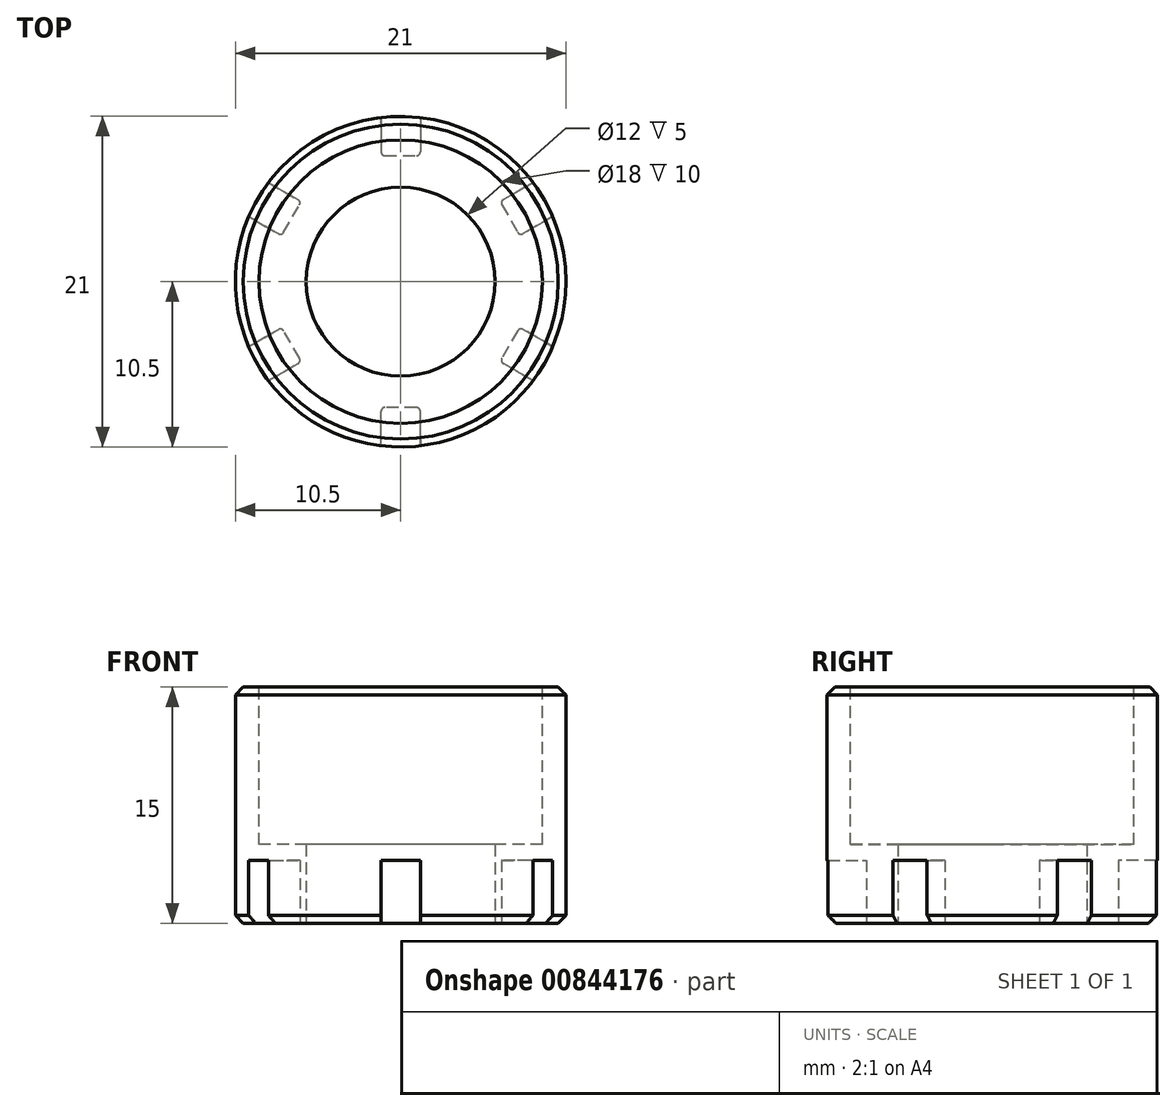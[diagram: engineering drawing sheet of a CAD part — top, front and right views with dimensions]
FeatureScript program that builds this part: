
annotation { "Feature Type Name" : "Feature", "Feature Type Description" : "" }
export const myFeature = defineFeature(function(context is Context, id is Id, definition is map)
    precondition{}
    {
        {
            var Q0;
            Q0=qCreatedBy(makeId("Top.planeOp"),FACE);
            var sketch = newSketch(context, id + "F0", { "sketchPlane" : qUnion([Q0])});
            skCircle(sketch, "E0", {"center": v(0, 0) * mm, "radius": 10.5 * mm});
            skCircle(sketch, "E1", {"center": v(0, 0) * mm, "radius": 6 * mm});
            skSolve(sketch);
        }
        {
            var Q0;
            Q0=makeQuery(id+"F0.imprint","IMPRINT",FACE,{"disambiguationData":[TD([[makeQuery(id+"F0.imprint","IMPRINT",EDGE,{"derivedFrom":sQuery(id+"F0.wireOp",EDGE,"E0")}),1.0]])]});
            extrude(context, id + "F1", {"entities" : qUnion([Q0]), "depth" : 15 * mm, "offsetDistance" : 25 * mm});
        }
        {
            var Q0;
            Q0=makeQuery(id+"F1.opExtrude","CAP_FACE",FACE,{"disambiguationData":[OSD([sQuery(id+"F0.wireOp",EDGE,"E0"),sQuery(id+"F0.wireOp",EDGE,"E1")])],"isStart":false});
            var sketch = newSketch(context, id + "F2", { "sketchPlane" : qUnion([Q0])});
            skCircle(sketch, "E2", {"center": v(0, 0) * mm, "radius": 9 * mm});
            skSolve(sketch);
        }
        {
            var Q0;
            Q0=makeQuery(id+"F2.imprint","IMPRINT",FACE,{"disambiguationData":[TD([[makeQuery(id+"F2.imprint","IMPRINT",EDGE,{"derivedFrom":sQuery(id+"F2.wireOp",EDGE,"E2")}),1.0]])]});
            extrude(context, id + "F3", {"entities" : qUnion([Q0]), "operationType" : NewBodyOperationType.REMOVE, "oppositeDirection" : true, "depth" : 10 * mm, "offsetDistance" : 25 * mm});
        }
        {
            var Q0;
            Q0=makeQuery(id+"F1.opExtrude","CAP_FACE",FACE,{"disambiguationData":[OSD([sQuery(id+"F0.wireOp",EDGE,"E0"),sQuery(id+"F0.wireOp",EDGE,"E1")])],"isStart":true});
            var sketch = newSketch(context, id + "F4", { "sketchPlane" : qUnion([Q0])});
            skLineSegment(sketch, "E3", {"start": v(0, 14.48) * mm, "end": v(0, 7.94) * mm, "construction": true});
            skLineSegment(sketch, "E4.bottom", {"start": v(1.25, 13) * mm, "end": v(-1.25, 13) * mm});
            skLineSegment(sketch, "E4.top", {"start": v(1, 8) * mm, "end": v(-1, 8) * mm});
            skLineSegment(sketch, "E4.left", {"start": v(1.25, 13) * mm, "end": v(1.25, 8.25) * mm});
            skLineSegment(sketch, "E4.right", {"start": v(-1.25, 13) * mm, "end": v(-1.25, 8.25) * mm});
            skPoint(sketch, "E4.middle", {"position": v(0, 10.5) * mm});
            skPoint(sketch, "E5.visualSharp", {"position": v(-1.25, 8) * mm});
            skArc(sketch, "E5.filletArc", {"start": v(-1.25, 8.25) * mm, "mid": v(-1.18, 8.07) * mm, "end": v(-1, 8) * mm});
            skPoint(sketch, "E6.visualSharp", {"position": v(1.25, 8) * mm});
            skArc(sketch, "E6.filletArc", {"start": v(1, 8) * mm, "mid": v(1.18, 8.07) * mm, "end": v(1.25, 8.25) * mm});
            skLineSegment(sketch, "E7.1.0", {"start": v(-10.63, 7.58) * mm, "end": v(-6.52, 5.2) * mm});
            skPoint(sketch, "E7.1.1", {"position": v(-9.1, 5.25) * mm});
            skPoint(sketch, "E7.1.2", {"position": v(-7.55, 2.92) * mm});
            skPoint(sketch, "E7.1.3", {"position": v(-6.3, 5.08) * mm});
            skLineSegment(sketch, "E7.1.4", {"start": v(-12.54, 7.24) * mm, "end": v(-6.88, 3.97) * mm, "construction": true});
            skLineSegment(sketch, "E7.1.5", {"start": v(-10.63, 7.58) * mm, "end": v(-11.88, 5.42) * mm});
            skLineSegment(sketch, "E7.1.6", {"start": v(-11.88, 5.42) * mm, "end": v(-7.77, 3.04) * mm});
            skLineSegment(sketch, "E7.1.7", {"start": v(-6.43, 4.87) * mm, "end": v(-7.43, 3.13) * mm});
            skArc(sketch, "E7.1.8", {"start": v(-7.77, 3.04) * mm, "mid": v(-7.58, 3.02) * mm, "end": v(-7.43, 3.13) * mm});
            skArc(sketch, "E7.1.9", {"start": v(-6.43, 4.87) * mm, "mid": v(-6.4, 5.06) * mm, "end": v(-6.52, 5.2) * mm});
            skLineSegment(sketch, "E7.2.0", {"start": v(-11.88, -5.42) * mm, "end": v(-7.77, -3.04) * mm});
            skPoint(sketch, "E7.2.1", {"position": v(-9.1, -5.25) * mm});
            skPoint(sketch, "E7.2.2", {"position": v(-6.3, -5.08) * mm});
            skPoint(sketch, "E7.2.3", {"position": v(-7.55, -2.92) * mm});
            skLineSegment(sketch, "E7.2.4", {"start": v(-12.54, -7.24) * mm, "end": v(-6.88, -3.97) * mm, "construction": true});
            skLineSegment(sketch, "E7.2.5", {"start": v(-11.88, -5.42) * mm, "end": v(-10.63, -7.58) * mm});
            skLineSegment(sketch, "E7.2.6", {"start": v(-10.63, -7.58) * mm, "end": v(-6.52, -5.2) * mm});
            skLineSegment(sketch, "E7.2.7", {"start": v(-7.43, -3.13) * mm, "end": v(-6.43, -4.87) * mm});
            skArc(sketch, "E7.2.8", {"start": v(-6.52, -5.2) * mm, "mid": v(-6.4, -5.06) * mm, "end": v(-6.43, -4.87) * mm});
            skArc(sketch, "E7.2.9", {"start": v(-7.43, -3.13) * mm, "mid": v(-7.58, -3.02) * mm, "end": v(-7.77, -3.04) * mm});
            skLineSegment(sketch, "E7.3.0", {"start": v(-1.25, -13) * mm, "end": v(-1.25, -8.25) * mm});
            skPoint(sketch, "E7.3.1", {"position": v(0, -10.5) * mm});
            skPoint(sketch, "E7.3.2", {"position": v(1.25, -8) * mm});
            skPoint(sketch, "E7.3.3", {"position": v(-1.25, -8) * mm});
            skLineSegment(sketch, "E7.3.4", {"start": v(0, -14.48) * mm, "end": v(0, -7.94) * mm, "construction": true});
            skLineSegment(sketch, "E7.3.5", {"start": v(-1.25, -13) * mm, "end": v(1.25, -13) * mm});
            skLineSegment(sketch, "E7.3.6", {"start": v(1.25, -13) * mm, "end": v(1.25, -8.25) * mm});
            skLineSegment(sketch, "E7.3.7", {"start": v(-1, -8) * mm, "end": v(1, -8) * mm});
            skArc(sketch, "E7.3.8", {"start": v(1.25, -8.25) * mm, "mid": v(1.18, -8.07) * mm, "end": v(1, -8) * mm});
            skArc(sketch, "E7.3.9", {"start": v(-1, -8) * mm, "mid": v(-1.18, -8.07) * mm, "end": v(-1.25, -8.25) * mm});
            skLineSegment(sketch, "E7.4.0", {"start": v(10.63, -7.58) * mm, "end": v(6.52, -5.2) * mm});
            skPoint(sketch, "E7.4.1", {"position": v(9.1, -5.25) * mm});
            skPoint(sketch, "E7.4.2", {"position": v(7.55, -2.92) * mm});
            skPoint(sketch, "E7.4.3", {"position": v(6.3, -5.08) * mm});
            skLineSegment(sketch, "E7.4.4", {"start": v(12.54, -7.24) * mm, "end": v(6.88, -3.97) * mm, "construction": true});
            skLineSegment(sketch, "E7.4.5", {"start": v(10.63, -7.58) * mm, "end": v(11.88, -5.42) * mm});
            skLineSegment(sketch, "E7.4.6", {"start": v(11.88, -5.42) * mm, "end": v(7.77, -3.04) * mm});
            skLineSegment(sketch, "E7.4.7", {"start": v(6.43, -4.87) * mm, "end": v(7.43, -3.13) * mm});
            skArc(sketch, "E7.4.8", {"start": v(7.77, -3.04) * mm, "mid": v(7.58, -3.02) * mm, "end": v(7.43, -3.13) * mm});
            skArc(sketch, "E7.4.9", {"start": v(6.43, -4.87) * mm, "mid": v(6.4, -5.06) * mm, "end": v(6.52, -5.2) * mm});
            skLineSegment(sketch, "E7.5.0", {"start": v(11.88, 5.42) * mm, "end": v(7.77, 3.04) * mm});
            skPoint(sketch, "E7.5.1", {"position": v(9.1, 5.25) * mm});
            skPoint(sketch, "E7.5.2", {"position": v(6.3, 5.08) * mm});
            skPoint(sketch, "E7.5.3", {"position": v(7.55, 2.92) * mm});
            skLineSegment(sketch, "E7.5.4", {"start": v(12.54, 7.24) * mm, "end": v(6.88, 3.97) * mm, "construction": true});
            skLineSegment(sketch, "E7.5.5", {"start": v(11.88, 5.42) * mm, "end": v(10.63, 7.58) * mm});
            skLineSegment(sketch, "E7.5.6", {"start": v(10.63, 7.58) * mm, "end": v(6.52, 5.2) * mm});
            skLineSegment(sketch, "E7.5.7", {"start": v(7.43, 3.13) * mm, "end": v(6.43, 4.87) * mm});
            skArc(sketch, "E7.5.8", {"start": v(6.52, 5.2) * mm, "mid": v(6.4, 5.06) * mm, "end": v(6.43, 4.87) * mm});
            skArc(sketch, "E7.5.9", {"start": v(7.43, 3.13) * mm, "mid": v(7.58, 3.02) * mm, "end": v(7.77, 3.04) * mm});
            skPoint(sketch, "E7.center", {"position": v(0, 0) * mm});
            skSolve(sketch);
        }
        {
            var Q0;
            Q0=qSketchRegion(id+"F4",true);
            extrude(context, id + "F5", {"entities" : qUnion([Q0]), "operationType" : NewBodyOperationType.REMOVE, "oppositeDirection" : true, "depth" : 4 * mm, "offsetDistance" : 25 * mm});
        }
        {
            var Q0;
            {var subQ0=sQuery(id+"F0.wireOp",EDGE,"E0");Q0=makeQuery(id+"F5.boolean.opBoolean","SPLIT",EDGE,{"disambiguationData":[TD([makeQuery(id+"F5.opExtrude","SWEPT_FACE",FACE,{"disambiguationData":[OSD([sQuery(id+"F4.wireOp",EDGE,"E4.right")])]})])],"derivedFrom":makeQuery(id+"F1.opExtrude","CAP_EDGE",EDGE,{"disambiguationData":[OSD([subQ0])],"isStart":true})});}
            var Q1;
            {var subQ0=sQuery(id+"F0.wireOp",EDGE,"E0");Q1=makeQuery(id+"F5.boolean.opBoolean","SPLIT",EDGE,{"disambiguationData":[TD([makeQuery(id+"F5.opExtrude","SWEPT_FACE",FACE,{"disambiguationData":[OSD([sQuery(id+"F4.wireOp",EDGE,"E4.left")])]})])],"derivedFrom":makeQuery(id+"F1.opExtrude","CAP_EDGE",EDGE,{"disambiguationData":[OSD([subQ0])],"isStart":true})});}
            var Q2;
            {var subQ0=sQuery(id+"F0.wireOp",EDGE,"E0");Q2=makeQuery(id+"F5.boolean.opBoolean","SPLIT",EDGE,{"disambiguationData":[TD([makeQuery(id+"F5.opExtrude","SWEPT_FACE",FACE,{"disambiguationData":[OSD([sQuery(id+"F4.wireOp",EDGE,"E7.4.6")])]})])],"derivedFrom":makeQuery(id+"F1.opExtrude","CAP_EDGE",EDGE,{"disambiguationData":[OSD([subQ0])],"isStart":true})});}
            var Q3;
            {var subQ0=sQuery(id+"F0.wireOp",EDGE,"E0");Q3=makeQuery(id+"F5.boolean.opBoolean","SPLIT",EDGE,{"disambiguationData":[TD([makeQuery(id+"F5.opExtrude","SWEPT_FACE",FACE,{"disambiguationData":[OSD([sQuery(id+"F4.wireOp",EDGE,"E7.3.6")])]})])],"derivedFrom":makeQuery(id+"F1.opExtrude","CAP_EDGE",EDGE,{"disambiguationData":[OSD([subQ0])],"isStart":true})});}
            var Q4;
            {var subQ0=sQuery(id+"F0.wireOp",EDGE,"E0");Q4=makeQuery(id+"F5.boolean.opBoolean","SPLIT",EDGE,{"disambiguationData":[TD([makeQuery(id+"F5.opExtrude","SWEPT_FACE",FACE,{"disambiguationData":[OSD([sQuery(id+"F4.wireOp",EDGE,"E7.2.6")])]})])],"derivedFrom":makeQuery(id+"F1.opExtrude","CAP_EDGE",EDGE,{"disambiguationData":[OSD([subQ0])],"isStart":true})});}
            var Q5;
            {var subQ0=sQuery(id+"F0.wireOp",EDGE,"E0");Q5=makeQuery(id+"F5.boolean.opBoolean","SPLIT",EDGE,{"disambiguationData":[TD([makeQuery(id+"F5.opExtrude","SWEPT_FACE",FACE,{"disambiguationData":[OSD([sQuery(id+"F4.wireOp",EDGE,"E7.1.6")])]})])],"derivedFrom":makeQuery(id+"F1.opExtrude","CAP_EDGE",EDGE,{"disambiguationData":[OSD([subQ0])],"isStart":true})});}
            chamfer(context, id + "F6", {"entities" : qUnion([Q0, Q1, Q2, Q3, Q4, Q5]), "width" : .5 * mm, "tangentPropagation" : true});
        }
        {
            var Q0;
            Q0=makeQuery(id+"F1.opExtrude","CAP_EDGE",EDGE,{"disambiguationData":[OSD([sQuery(id+"F0.wireOp",EDGE,"E0")])],"isStart":false});
            chamfer(context, id + "F7", {"entities" : qUnion([Q0]), "width" : .5 * mm, "tangentPropagation" : true});
        }
    });
